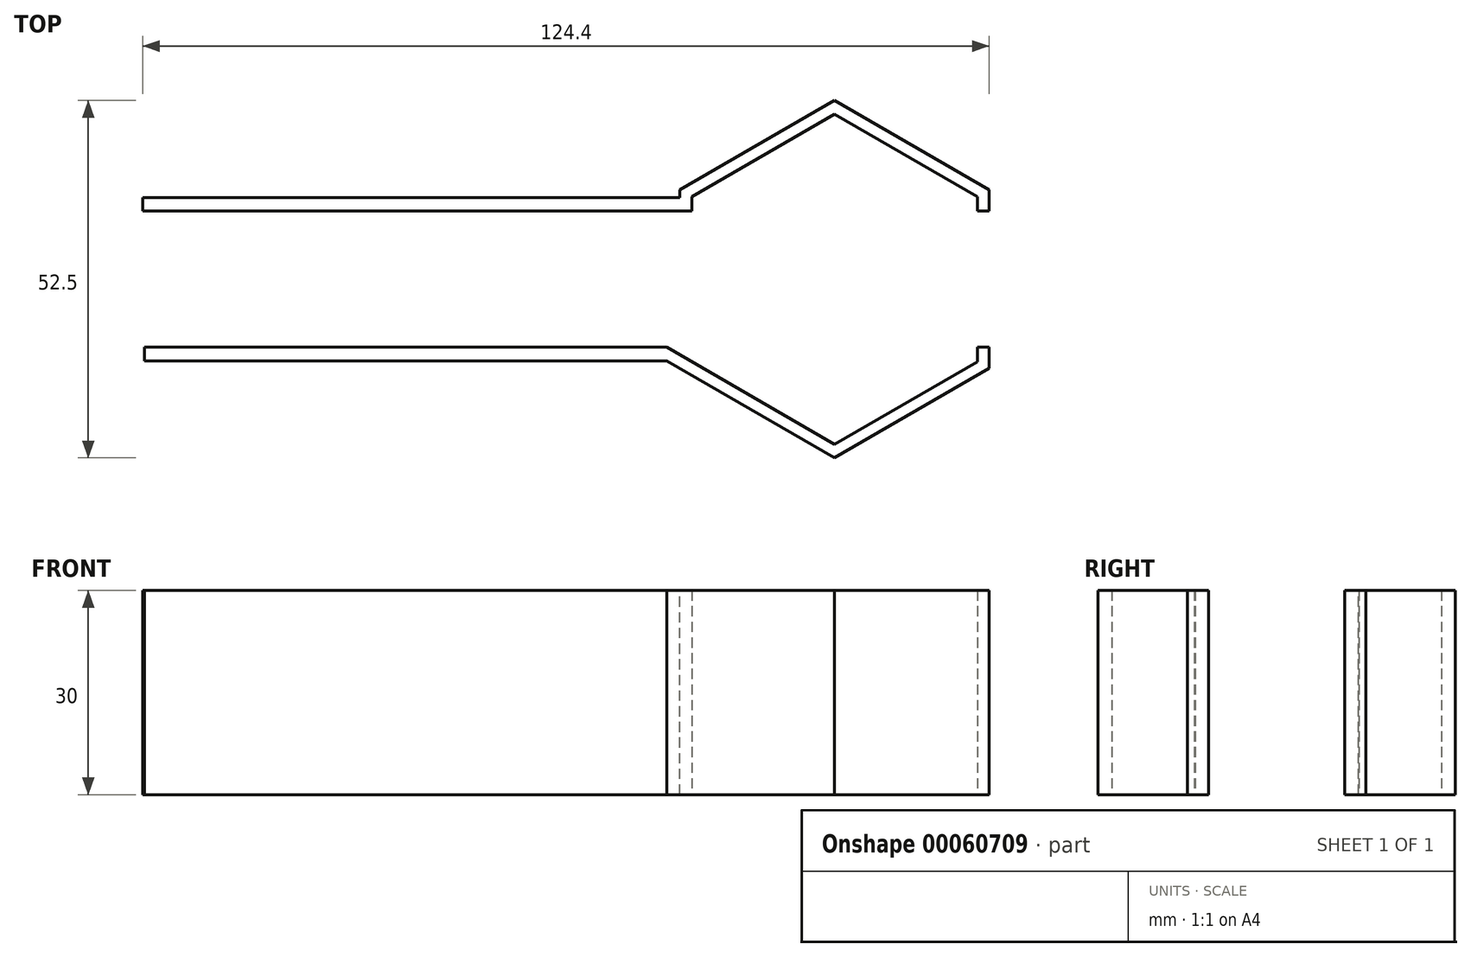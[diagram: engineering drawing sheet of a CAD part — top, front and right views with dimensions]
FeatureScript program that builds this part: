
annotation { "Feature Type Name" : "Feature", "Feature Type Description" : "" }
export const myFeature = defineFeature(function(context is Context, id is Id, definition is map)
    precondition{}
    {
        {
            var Q0;
            Q0=qCreatedBy(makeId("Top.planeOp"),FACE);
            var sketch = newSketch(context, id + "F0", { "sketchPlane" : qUnion([Q0])});
            skCircle(sketch, "E0.cCircle", {"center": v(0, 0) * mm, "radius": 21 * mm, "construction": true});
            skLineSegment(sketch, "E0.0", {"start": v(21, 12.12) * mm, "end": v(21, -12.12) * mm});
            skLineSegment(sketch, "E0.1", {"start": v(21, -12.12) * mm, "end": v(0, -24.25) * mm});
            skLineSegment(sketch, "E0.2", {"start": v(0, -24.25) * mm, "end": v(-21, -12.12) * mm});
            skLineSegment(sketch, "E0.3", {"start": v(-21, -12.12) * mm, "end": v(-21, 12.12) * mm});
            skLineSegment(sketch, "E0.4", {"start": v(-21, 12.12) * mm, "end": v(0, 24.25) * mm});
            skLineSegment(sketch, "E0.5", {"start": v(0, 24.25) * mm, "end": v(21, 12.12) * mm});
            skPoint(sketch, "E0.0.midPoint", {"position": v(21, 0) * mm});
            skSolve(sketch);
        }
        {
            var Q0;
            Q0=makeQuery(id+"F0.imprint","IMPRINT",FACE,{"disambiguationData":[TD([[makeQuery(id+"F0.imprint","IMPRINT",EDGE,{"derivedFrom":sQuery(id+"F0.wireOp",EDGE,"E0.0")}),-1.0]])]});
            extrude(context, id + "F1", {"entities" : qUnion([Q0]), "endBound" : BoundingType.SYMMETRIC, "depth" : 50 * mm});
        }
        {
            var Q0;
            Q0=qCreatedBy(makeId("Top.planeOp"),FACE);
            var sketch = newSketch(context, id + "F2", { "sketchPlane" : qUnion([Q0])});
            skCircle(sketch, "E1.cCircle", {"center": v(0, 0) * mm, "radius": 22.73 * mm, "construction": true});
            skLineSegment(sketch, "E1.0", {"start": v(22.73, -13.12) * mm, "end": v(0, -26.25) * mm});
            skLineSegment(sketch, "E1.1", {"start": v(0, -26.25) * mm, "end": v(-22.73, -13.12) * mm});
            skLineSegment(sketch, "E1.2", {"start": v(-22.73, -13.12) * mm, "end": v(-22.73, 13.12) * mm});
            skLineSegment(sketch, "E1.3", {"start": v(-22.73, 13.12) * mm, "end": v(0, 26.25) * mm});
            skLineSegment(sketch, "E1.4", {"start": v(0, 26.25) * mm, "end": v(22.73, 13.12) * mm});
            skLineSegment(sketch, "E1.5", {"start": v(22.73, 13.12) * mm, "end": v(22.73, -13.12) * mm});
            skPoint(sketch, "E1.0.midPoint", {"position": v(11.37, -19.69) * mm});
            skSolve(sketch);
        }
        {
            var Q0;
            Q0=makeQuery(id+"F2.imprint","IMPRINT",FACE,{"disambiguationData":[TD([[makeQuery(id+"F2.imprint","IMPRINT",EDGE,{"derivedFrom":sQuery(id+"F2.wireOp",EDGE,"E1.0")}),-1.0]])]});
            extrude(context, id + "F3", {"entities" : qUnion([Q0]), "endBound" : BoundingType.SYMMETRIC, "depth" : 30 * mm});
        }
        {
            var Q0;
            Q0=makeQuery(id+"F1.opExtrude","SWEPT_BODY",BODY,{"disambiguationData":[OSD([sQuery(id+"F0.wireOp",EDGE,"E0.0"),sQuery(id+"F0.wireOp",EDGE,"E0.1"),sQuery(id+"F0.wireOp",EDGE,"E0.2"),sQuery(id+"F0.wireOp",EDGE,"E0.3"),sQuery(id+"F0.wireOp",EDGE,"E0.4"),sQuery(id+"F0.wireOp",EDGE,"E0.5")])]});
            var Q1;
            Q1=makeQuery(id+"F3.opExtrude","SWEPT_BODY",BODY,{"disambiguationData":[OSD([sQuery(id+"F2.wireOp",EDGE,"E1.0"),sQuery(id+"F2.wireOp",EDGE,"E1.1"),sQuery(id+"F2.wireOp",EDGE,"E1.2"),sQuery(id+"F2.wireOp",EDGE,"E1.3"),sQuery(id+"F2.wireOp",EDGE,"E1.4"),sQuery(id+"F2.wireOp",EDGE,"E1.5")])]});
            booleanBodies(context, id + "F4", {"operationType" : BooleanOperationType.SUBTRACTION, "tools" : qUnion([Q0]), "targets" : qUnion([Q1])});
        }
        {
            var Q0;
            Q0=qCreatedBy(makeId("Top.planeOp"),FACE);
            var sketch = newSketch(context, id + "F5", { "sketchPlane" : qUnion([Q0])});
            skLineSegment(sketch, "E2.rect.bottom", {"start": v(40.93, -10) * mm, "end": v(-40.93, -10) * mm});
            skLineSegment(sketch, "E2.rect.top", {"start": v(40.93, 10) * mm, "end": v(-40.93, 10) * mm});
            skLineSegment(sketch, "E2.rect.left", {"start": v(40.93, -10) * mm, "end": v(40.93, 10) * mm});
            skLineSegment(sketch, "E2.rect.right", {"start": v(-40.93, -10) * mm, "end": v(-40.93, 10) * mm});
            skPoint(sketch, "E2.rect.middle", {"position": v(0, 0) * mm});
            skSolve(sketch);
        }
        {
            var Q0;
            Q0 = qSketchRegion(id + "F5", true);
            extrude(context, id + "F6", {"entities" : qUnion([Q0]), "operationType" : NewBodyOperationType.REMOVE, "endBound" : BoundingType.SYMMETRIC, "oppositeDirection" : true, "depth" : 30 * mm});
        }
        {
            var Q0;
            Q0=qCreatedBy(makeId("Top.planeOp"),FACE);
            var sketch = newSketch(context, id + "F7", { "sketchPlane" : qUnion([Q0])});
            skLineSegment(sketch, "E3", {"start": v(-13.49, -18.46) * mm, "end": v(-24.68, -12) * mm});
            skLineSegment(sketch, "E4", {"start": v(-12.64, -16.95) * mm, "end": v(-24.68, -10) * mm});
            skLineSegment(sketch, "E5.bottom", {"start": v(-22.73, -12) * mm, "end": v(-101.4, -12) * mm});
            skLineSegment(sketch, "E5.top", {"start": v(-22.73, -10) * mm, "end": v(-101.4, -10) * mm});
            skLineSegment(sketch, "E5.left", {"start": v(-22.73, -12) * mm, "end": v(-22.73, -10) * mm});
            skLineSegment(sketch, "E5.right", {"start": v(-101.4, -12) * mm, "end": v(-101.4, -10) * mm});
            skLineSegment(sketch, "E6", {"start": v(29.3, -10) * mm, "end": v(-70.3, -10) * mm, "construction": true});
            skLineSegment(sketch, "E7", {"start": v(-24.68, -12) * mm, "end": v(-24.68, -10) * mm});
            skLineSegment(sketch, "E8", {"start": v(-13.49, -18.46) * mm, "end": v(-12.64, -16.95) * mm});
            skSolve(sketch);
        }
        {
            var Q0;
            {var subQ2=sQuery(id+"F7.wireOp",EDGE,"E5.right");Q0=makeQuery(id+"F7.imprint","IMPRINT",FACE,{"disambiguationData":[TD([[makeQuery(id+"F7.imprint","IMPRINT",EDGE,{"derivedFrom":subQ2}),-1.0]])]});}
            var Q1;
            {var subQ0=sQuery(id+"F7.wireOp",EDGE,"E7");Q1=makeQuery(id+"F7.imprint","IMPRINT",FACE,{"disambiguationData":[TD([[makeQuery(id+"F7.imprint","IMPRINT",EDGE,{"derivedFrom":subQ0}),-1.0]])]});}
            var Q2;
            {var subQ5=sQuery(id+"F7.wireOp",EDGE,"E3");Q2=makeQuery(id+"F7.imprint","IMPRINT",FACE,{"disambiguationData":[TD([[makeQuery(id+"F7.imprint","IMPRINT",EDGE,{"derivedFrom":subQ5}),-1.0]])]});}
            extrude(context, id + "F8", {"entities" : qUnion([Q0, Q1, Q2]), "operationType" : NewBodyOperationType.ADD, "endBound" : BoundingType.SYMMETRIC, "depth" : 30 * mm});
        }
        {
            var Q0;
            Q0=qCreatedBy(makeId("Top.planeOp"),FACE);
            var sketch = newSketch(context, id + "F9", { "sketchPlane" : qUnion([Q0])});
            skLineSegment(sketch, "E9", {"start": v(-19.46, -13.01) * mm, "end": v(-25.78, -9.37) * mm});
            skLineSegment(sketch, "E10", {"start": v(-25.78, -9.37) * mm, "end": v(-18.3, -9.37) * mm});
            skLineSegment(sketch, "E11", {"start": v(-18.3, -9.37) * mm, "end": v(-19.46, -13.01) * mm});
            skSolve(sketch);
        }
        {
            var Q0;
            Q0=makeQuery(id+"F9.imprint","IMPRINT",FACE,{"disambiguationData":[TD([[makeQuery(id+"F9.imprint","IMPRINT",EDGE,{"derivedFrom":sQuery(id+"F9.wireOp",EDGE,"E9")}),-1.0]])]});
            extrude(context, id + "F10", {"entities" : qUnion([Q0]), "operationType" : NewBodyOperationType.REMOVE, "endBound" : BoundingType.SYMMETRIC, "oppositeDirection" : true, "depth" : 30 * mm});
        }
        {
            var Q0;
            Q0=qCreatedBy(makeId("Top.planeOp"),FACE);
            var sketch = newSketch(context, id + "F11", { "sketchPlane" : qUnion([Q0])});
            skLineSegment(sketch, "E12.bottom", {"start": v(-21, 10) * mm, "end": v(-101.67, 10) * mm});
            skLineSegment(sketch, "E12.top", {"start": v(-21, 12) * mm, "end": v(-101.67, 12) * mm});
            skLineSegment(sketch, "E12.left", {"start": v(-21, 10) * mm, "end": v(-21, 12) * mm});
            skLineSegment(sketch, "E12.right", {"start": v(-101.67, 10) * mm, "end": v(-101.67, 12) * mm});
            skSolve(sketch);
        }
        {
            var Q0;
            Q0=makeQuery(id+"F11.imprint","IMPRINT",FACE,{"disambiguationData":[TD([[makeQuery(id+"F11.imprint","IMPRINT",EDGE,{"derivedFrom":sQuery(id+"F11.wireOp",EDGE,"E12.bottom")}),-1.0]])]});
            extrude(context, id + "F12", {"entities" : qUnion([Q0]), "operationType" : NewBodyOperationType.ADD, "endBound" : BoundingType.SYMMETRIC, "depth" : 30 * mm});
        }
    });
